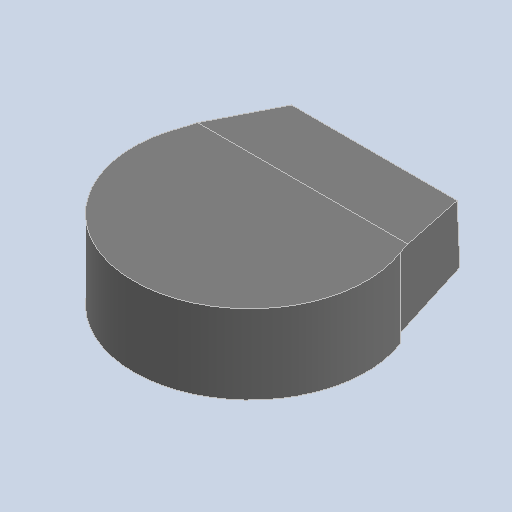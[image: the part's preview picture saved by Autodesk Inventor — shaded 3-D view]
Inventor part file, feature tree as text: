
AUTODESK INVENTOR PART (.ipt)
format: ipt  version: 2022 (Build 260153000, 153)  size: 236,544 bytes
history: native  units: mm
features: sketch x11, extrude x10, chamfer x2, plane x1
ambient origin geometry x8: Origin, YZ Plane, XZ Plane, XY Plane, X Axis, Y Axis, Z Axis, Center Point
bodies: Solid1 (feature_tree)
feature tree (24):
  extrude  "Extrusion1"  Depth=55.2mm
  chamfer  "Chamfer1"  Distance=30.0mm
  chamfer  "Chamfer2"  Distance=30.0mm Angle=45.0deg
  extrude  "Extrusion2"  Depth=4.0mm
  extrude  "Extrusion3"  Depth=30.0mm
  extrude  "Extrusion4"  Depth=4.0mm
  extrude  "Extrusion5"  Depth=30.0mm
  extrude  "Extrusion6"  Depth=5.0mm
  extrude  "Extrusion7"  Depth=5.0mm TaperAngle=0.0deg
  extrude  "Extrusion8"  Depth=5.0mm
  sketch  "Sketch9"  dims[d18=73.6mm d19=4.0mm]
  plane  "Work Plane1"
  extrude  "Extrusion9"  Depth=5.0mm
  extrude  "Extrusion10"  Depth=5.0mm TaperAngle=0.0deg
  sketch  "Sketch1"  dims[d0=100.05mm d1=55.2mm]
  sketch  "Sketch2"  dims[d2=35.075mm]
  sketch  "Sketch3"  dims[d3=35.075mm]
  sketch  "Sketch4"  dims[d4=67.85mm]
  sketch  "Sketch5"  dims[d5=2.0mm]
  sketch  "Sketch6"  dims[d6=2.0mm d7=30.0mm d8=0.0mm d9=2.0mm d10=30.0mm d11=45.0deg]
  sketch  "Sketch7"  dims[d12=4.0mm d13=30.5mm d14=45.0deg d15=2.0mm]
  sketch  "Sketch8"  dims[d16=59.0mm d17=30.0mm]
  sketch  "Sketch12"  dims[d20=4.0mm d21=0.0mm d22=30.0mm]
  sketch  "Sketch13"  dims[d24=74.75mm d25=2.5mm d26=5.0mm d27=0.0mm d28=5.0mm d29=3.5mm d30=5.0mm d31=0.0mm d32=30.0mm d33=0.0mm d34=10.0mm d35=0.0mm d36=2.5mm d37=5.0mm d38=0.0mm d39=3.0mm d40=3.0mm d41=5.0mm d42=0.0mm d43=3.5mm d44=3.5mm d47=3.0mm d48=3.0mm d49=3.0mm d50=3.0mm d51=50.0mm d52=10.0mm d53=0.0mm d54=0.0mm d55=5.0mm d56=5.0mm d57=5.0mm d58=5.0mm d59=4.5mm d60=57.0mm d61=2.0mm d62=0.0mm d63=0.0mm]
